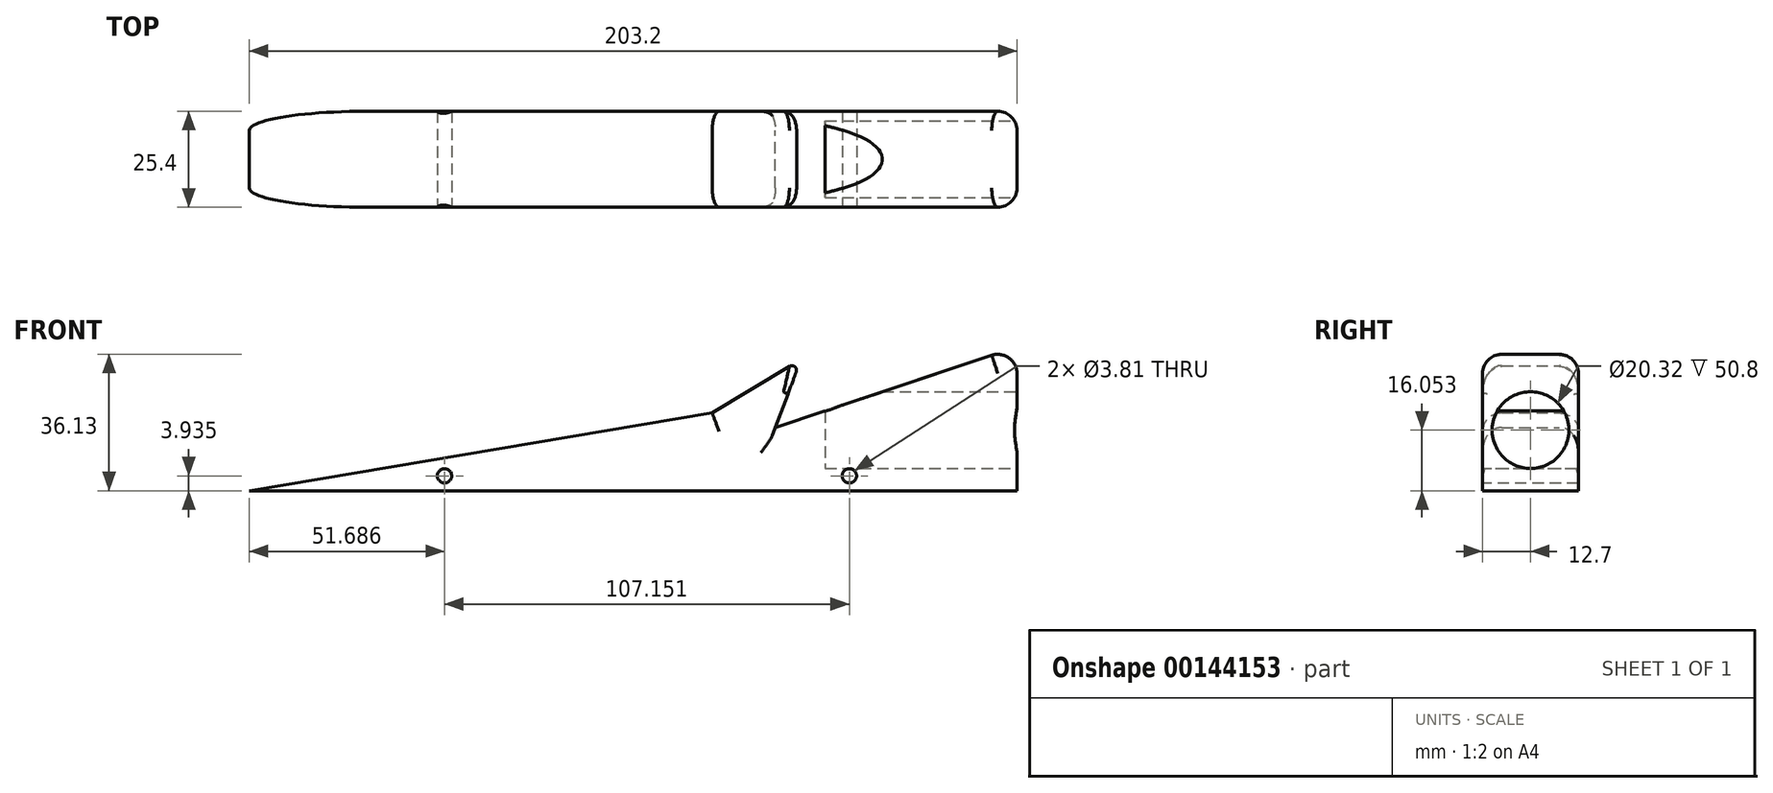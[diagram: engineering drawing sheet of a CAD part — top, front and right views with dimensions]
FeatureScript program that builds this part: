
annotation { "Feature Type Name" : "Feature", "Feature Type Description" : "" }
export const myFeature = defineFeature(function(context is Context, id is Id, definition is map)
    precondition{}
    {
        {
            var Q0;
            Q0=qCreatedBy(makeId("Front.planeOp"),FACE);
            var sketch = newSketch(context, id + "F0", { "sketchPlane" : qUnion([Q0])});
            skLineSegment(sketch, "E0", {"start": v(-98.76, 0) * mm, "end": v(104.44, 0) * mm});
            skLineSegment(sketch, "E1", {"start": v(104.44, 0) * mm, "end": v(104.44, 38.1) * mm});
            skLineSegment(sketch, "E2", {"start": v(-98.76, 0) * mm, "end": v(23.78, 20.59) * mm});
            skLineSegment(sketch, "E3", {"start": v(23.78, 20.59) * mm, "end": v(47.26, 34.81) * mm});
            skLineSegment(sketch, "E4", {"start": v(47.26, 34.81) * mm, "end": v(40.49, 16.75) * mm});
            skLineSegment(sketch, "E5", {"start": v(40.49, 16.75) * mm, "end": v(104.44, 38.1) * mm});
            skSolve(sketch);
        }
        {
            var Q0;
            Q0=qSketchRegion(id+"F0",true);
            extrude(context, id + "F1", {"entities" : qUnion([Q0]), "depth" : 25.4 * mm});
        }
        {
            var Q0;
            Q0=makeQuery(id+"F1.opExtrude","SWEPT_FACE",FACE,{"disambiguationData":[OSD([sQuery(id+"F0.wireOp",EDGE,"E1")])]});
            var sketch = newSketch(context, id + "F2", { "sketchPlane" : qUnion([Q0])});
            skCircle(sketch, "E6", {"center": v(-12.7, 16.05) * mm, "radius": 10.16 * mm});
            skSolve(sketch);
        }
        {
            var Q0;
            Q0=makeQuery(id+"F1.opExtrude","CAP_FACE",FACE,{"disambiguationData":[OSD([sQuery(id+"F0.wireOp",EDGE,"E0"),sQuery(id+"F0.wireOp",EDGE,"E1"),sQuery(id+"F0.wireOp",EDGE,"E2"),sQuery(id+"F0.wireOp",EDGE,"E3"),sQuery(id+"F0.wireOp",EDGE,"E4"),sQuery(id+"F0.wireOp",EDGE,"E5")])],"isStart":false});
            var sketch = newSketch(context, id + "F3", { "sketchPlane" : qUnion([Q0])});
            skCircle(sketch, "E7", {"center": v(-47.07, 3.93) * mm, "radius": 1.9 * mm});
            skCircle(sketch, "E8", {"center": v(60.08, 3.93) * mm, "radius": 1.9 * mm});
            skSolve(sketch);
        }
        {
            var Q0;
            Q0=qSketchRegion(id+"F3",true);
            extrude(context, id + "F4", {"entities" : qUnion([Q0]), "operationType" : NewBodyOperationType.REMOVE, "oppositeDirection" : true, "depth" : 25.4 * mm});
        }
        {
            var Q0;
            Q0=qSketchRegion(id+"F2",true);
            extrude(context, id + "F5", {"entities" : qUnion([Q0]), "operationType" : NewBodyOperationType.REMOVE, "oppositeDirection" : true, "depth" : 50.8 * mm});
        }
        {
            var Q0;
            Q0=makeQuery(id+"F1.opExtrude","CAP_EDGE",EDGE,{"disambiguationData":[OSD([sQuery(id+"F0.wireOp",EDGE,"E2")])],"isStart":false});
            var Q1;
            Q1=makeQuery(id+"F1.opExtrude","CAP_EDGE",EDGE,{"disambiguationData":[OSD([sQuery(id+"F0.wireOp",EDGE,"E2")])],"isStart":true});
            var Q2;
            Q2=makeQuery(id+"F1.opExtrude","CAP_EDGE",EDGE,{"disambiguationData":[OSD([sQuery(id+"F0.wireOp",EDGE,"E3")])],"isStart":true});
            var Q3;
            Q3=makeQuery(id+"F1.opExtrude","CAP_EDGE",EDGE,{"disambiguationData":[OSD([sQuery(id+"F0.wireOp",EDGE,"E3")])],"isStart":false});
            fillet(context, id + "F6", {"entities" : qUnion([Q0, Q1, Q2, Q3]), "radius" : 5.08 * mm, "tangentPropagation" : true, "allowEdgeOverflow" : false});
        }
        {
            var Q0;
            Q0=makeQuery(id+"F1.opExtrude","CAP_EDGE",EDGE,{"disambiguationData":[OSD([sQuery(id+"F0.wireOp",EDGE,"E5")])],"isStart":false});
            var Q1;
            Q1=makeQuery(id+"F1.opExtrude","CAP_EDGE",EDGE,{"disambiguationData":[OSD([sQuery(id+"F0.wireOp",EDGE,"E5")])],"isStart":true});
            fillet(context, id + "F7", {"entities" : qUnion([Q0, Q1]), "radius" : 5.08 * mm, "tangentPropagation" : true, "allowEdgeOverflow" : false});
        }
        {
            var Q0;
            Q0=makeQuery(id+"F1.opExtrude","SWEPT_EDGE",EDGE,{"disambiguationData":[OSD([sQuery(id+"F0.wireOp",EDGE,"E3"),sQuery(id+"F0.wireOp",EDGE,"E4")])]});
            fillet(context, id + "F8", {"entities" : qUnion([Q0]), "radius" : 1.24 * mm, "tangentPropagation" : true, "allowEdgeOverflow" : false});
        }
        {
            var Q0;
            Q0=makeQuery(id+"F7.opFillet","BLEND_EDGE",EDGE,{"blendedFrom":[makeQuery(id+"F1.opExtrude","CAP_EDGE",EDGE,{"disambiguationData":[OSD([sQuery(id+"F0.wireOp",EDGE,"E5")])],"isStart":false}),makeQuery(id+"F1.opExtrude","SWEPT_FACE",FACE,{"disambiguationData":[OSD([sQuery(id+"F0.wireOp",EDGE,"E1")])]})],"blendedInto":[makeQuery(id+"F1.opExtrude","SWEPT_FACE",FACE,{"disambiguationData":[OSD([sQuery(id+"F0.wireOp",EDGE,"E1")])]})]});
            var Q1;
            Q1=makeQuery(id+"F1.opExtrude","SWEPT_EDGE",EDGE,{"disambiguationData":[OSD([sQuery(id+"F0.wireOp",EDGE,"E1"),sQuery(id+"F0.wireOp",EDGE,"E5")])]});
            var Q2;
            Q2=makeQuery(id+"F7.opFillet","BLEND_EDGE",EDGE,{"blendedFrom":[makeQuery(id+"F1.opExtrude","CAP_EDGE",EDGE,{"disambiguationData":[OSD([sQuery(id+"F0.wireOp",EDGE,"E5")])],"isStart":true}),makeQuery(id+"F1.opExtrude","SWEPT_FACE",FACE,{"disambiguationData":[OSD([sQuery(id+"F0.wireOp",EDGE,"E1")])]})],"blendedInto":[makeQuery(id+"F1.opExtrude","SWEPT_FACE",FACE,{"disambiguationData":[OSD([sQuery(id+"F0.wireOp",EDGE,"E1")])]})]});
            fillet(context, id + "F9", {"entities" : qUnion([Q0, Q1, Q2]), "radius" : 5.08 * mm, "tangentPropagation" : true, "allowEdgeOverflow" : false});
        }
    });
